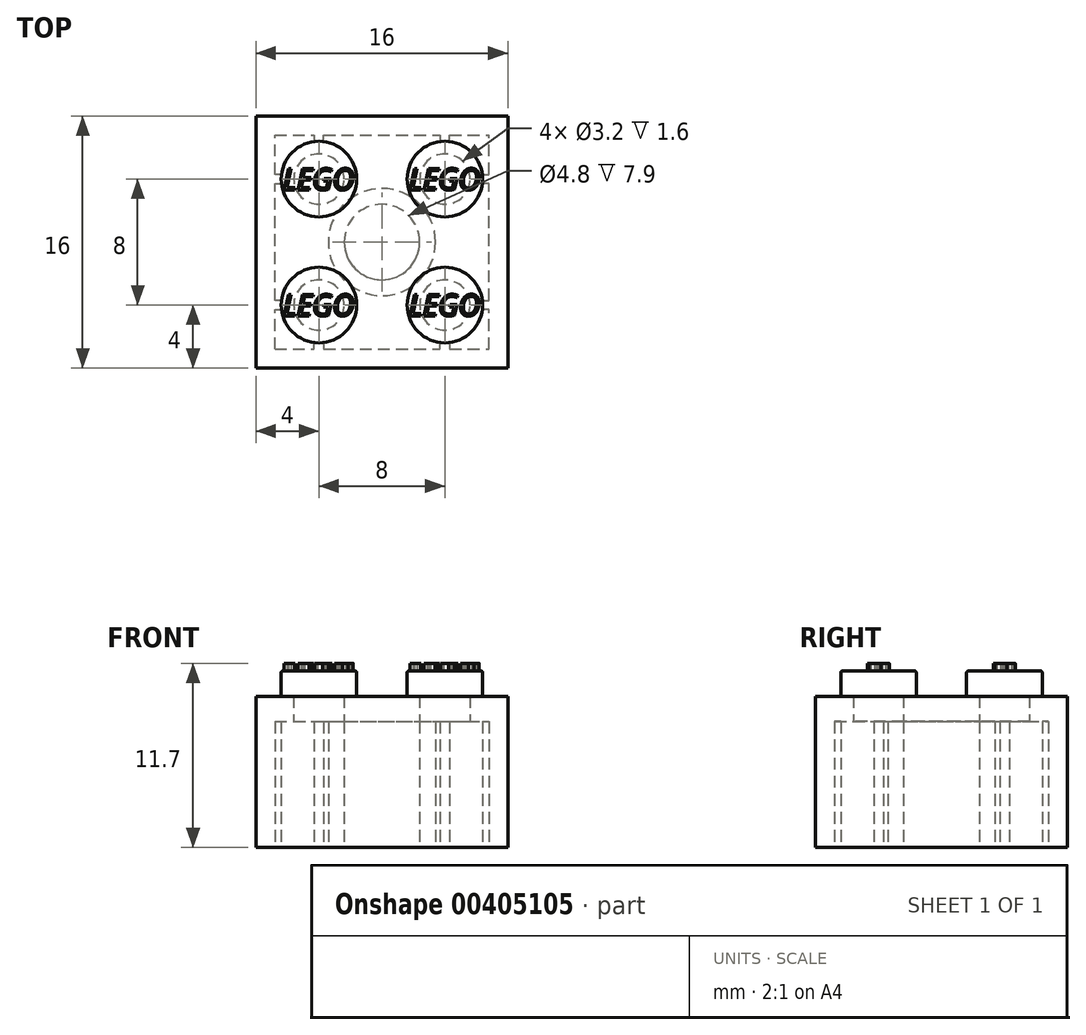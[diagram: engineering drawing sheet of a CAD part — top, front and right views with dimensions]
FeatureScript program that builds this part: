
annotation { "Feature Type Name" : "Feature", "Feature Type Description" : "" }
export const myFeature = defineFeature(function(context is Context, id is Id, definition is map)
    precondition{}
    {
        {
            var Q0;
            Q0=qCreatedBy(makeId("Top.planeOp"),FACE);
            var sketch = newSketch(context, id + "F0", { "sketchPlane" : qUnion([Q0])});
            skLineSegment(sketch, "E0.bottom", {"start": v(0, 0) * mm, "end": v(16, 0) * mm});
            skLineSegment(sketch, "E0.top", {"start": v(0, 16) * mm, "end": v(16, 16) * mm});
            skLineSegment(sketch, "E0.left", {"start": v(0, 0) * mm, "end": v(0, 16) * mm});
            skLineSegment(sketch, "E0.right", {"start": v(16, 0) * mm, "end": v(16, 16) * mm});
            skSolve(sketch);
        }
        {
            var Q0;
            Q0 = qSketchRegion(id + "F0", true);
            var Q1;
            Q1 = qConstructionFilter(qBodyType(qCreatedBy(id + "F0" ,EDGE), BodyType.WIRE), ConstructionObject.NO);
            extrude(context, id + "F1", {"entities" : qUnion([Q0]), "surfaceEntities" : qUnion([Q1]), "depth" : 9.6 * mm});
        }
        {
            var Q0;
            Q0=makeQuery(id+"F1.opExtrude","CAP_FACE",FACE,{"disambiguationData":[OSD([sQuery(id+"F0.wireOp",EDGE,"E0.bottom"),sQuery(id+"F0.wireOp",EDGE,"E0.top"),sQuery(id+"F0.wireOp",EDGE,"E0.left"),sQuery(id+"F0.wireOp",EDGE,"E0.right")])],"isStart":false});
            var sketch = newSketch(context, id + "F2", { "sketchPlane" : qUnion([Q0])});
            skLineSegment(sketch, "E1", {"start": v(0, 12) * mm, "end": v(16, 12) * mm, "construction": true});
            skLineSegment(sketch, "E2", {"start": v(4, 16) * mm, "end": v(4, 0) * mm, "construction": true});
            skLineSegment(sketch, "E3", {"start": v(12, 16) * mm, "end": v(12, 0) * mm, "construction": true});
            skLineSegment(sketch, "E4", {"start": v(0, 4) * mm, "end": v(16, 4) * mm, "construction": true});
            skCircle(sketch, "E5", {"center": v(4, 12) * mm, "radius": 2.4 * mm});
            skCircle(sketch, "E6", {"center": v(4, 4) * mm, "radius": 2.4 * mm});
            skCircle(sketch, "E7", {"center": v(12, 12) * mm, "radius": 2.4 * mm});
            skCircle(sketch, "E8", {"center": v(12, 4) * mm, "radius": 2.4 * mm});
            skSolve(sketch);
        }
        {
            var Q0;
            Q0 = qSketchRegion(id + "F2", true);
            extrude(context, id + "F3", {"entities" : qUnion([Q0]), "operationType" : NewBodyOperationType.ADD, "depth" : 1.6 * mm});
        }
        {
            var Q0;
            Q0=makeQuery(id+"F1.opExtrude","CAP_FACE",FACE,{"disambiguationData":[OSD([sQuery(id+"F0.wireOp",EDGE,"E0.bottom"),sQuery(id+"F0.wireOp",EDGE,"E0.top"),sQuery(id+"F0.wireOp",EDGE,"E0.left"),sQuery(id+"F0.wireOp",EDGE,"E0.right")])],"isStart":true});
            var sketch = newSketch(context, id + "F4", { "sketchPlane" : qUnion([Q0])});
            skLineSegment(sketch, "E9.bottom", {"start": v(0, 0) * mm, "end": v(16, 0) * mm, "construction": true});
            skLineSegment(sketch, "E9.top", {"start": v(0, -16) * mm, "end": v(16, -16) * mm, "construction": true});
            skLineSegment(sketch, "E9.left", {"start": v(0, 0) * mm, "end": v(0, -16) * mm, "construction": true});
            skLineSegment(sketch, "E9.right", {"start": v(16, 0) * mm, "end": v(16, -16) * mm, "construction": true});
            skLineSegment(sketch, "E10.0", {"start": v(1.2, -1.2) * mm, "end": v(14.8, -1.2) * mm});
            skLineSegment(sketch, "E10.1", {"start": v(1.2, -1.2) * mm, "end": v(1.2, -14.8) * mm});
            skLineSegment(sketch, "E10.2", {"start": v(1.2, -14.8) * mm, "end": v(14.8, -14.8) * mm});
            skLineSegment(sketch, "E10.3", {"start": v(14.8, -1.2) * mm, "end": v(14.8, -14.8) * mm});
            skLineSegment(sketch, "E11", {"start": v(1.2, -1.2) * mm, "end": v(14.8, -14.8) * mm, "construction": true});
            skLineSegment(sketch, "E12", {"start": v(1.2, -14.8) * mm, "end": v(14.8, -1.2) * mm, "construction": true});
            skCircle(sketch, "E13", {"center": v(8, -8) * mm, "radius": 3.4 * mm});
            skCircle(sketch, "E14", {"center": v(8, -8) * mm, "radius": 2.4 * mm});
            skLineSegment(sketch, "E15", {"start": v(1.2, -4) * mm, "end": v(14.8, -4) * mm, "construction": true});
            skLineSegment(sketch, "E16", {"start": v(14.8, -12) * mm, "end": v(1.2, -12) * mm, "construction": true});
            skLineSegment(sketch, "E17", {"start": v(4, -1.2) * mm, "end": v(4, -14.8) * mm, "construction": true});
            skLineSegment(sketch, "E18", {"start": v(12, -1.2) * mm, "end": v(12, -14.8) * mm, "construction": true});
            skLineSegment(sketch, "E19", {"start": v(3.7, -1.2) * mm, "end": v(3.7, -1.6) * mm});
            skLineSegment(sketch, "E20", {"start": v(3.7, -1.6) * mm, "end": v(4.3, -1.6) * mm});
            skLineSegment(sketch, "E21", {"start": v(4.3, -1.6) * mm, "end": v(4.3, -1.2) * mm});
            skLineSegment(sketch, "E22", {"start": v(11.7, -1.2) * mm, "end": v(11.7, -1.6) * mm});
            skLineSegment(sketch, "E23", {"start": v(11.7, -1.6) * mm, "end": v(12.3, -1.6) * mm});
            skLineSegment(sketch, "E24", {"start": v(12.3, -1.6) * mm, "end": v(12.3, -1.2) * mm});
            skLineSegment(sketch, "E25", {"start": v(1.2, -8) * mm, "end": v(14.8, -8) * mm, "construction": true});
            skLineSegment(sketch, "E26.MirrorCS", {"start": v(11.7, -14.8) * mm, "end": v(11.7, -14.4) * mm});
            skLineSegment(sketch, "E27.MirrorCS", {"start": v(11.7, -14.4) * mm, "end": v(12.3, -14.4) * mm});
            skLineSegment(sketch, "E28.MirrorCS", {"start": v(12.3, -14.4) * mm, "end": v(12.3, -14.8) * mm});
            skLineSegment(sketch, "E29.MirrorCS", {"start": v(4.3, -14.4) * mm, "end": v(4.3, -14.8) * mm});
            skLineSegment(sketch, "E30.MirrorCS", {"start": v(3.7, -14.8) * mm, "end": v(3.7, -14.4) * mm});
            skLineSegment(sketch, "E31.MirrorCS", {"start": v(3.7, -14.4) * mm, "end": v(4.3, -14.4) * mm});
            skLineSegment(sketch, "E32", {"start": v(8, -1.2) * mm, "end": v(8, -14.8) * mm, "construction": true});
            skLineSegment(sketch, "E33", {"start": v(1.2, -3.7) * mm, "end": v(1.6, -3.7) * mm});
            skLineSegment(sketch, "E34", {"start": v(1.6, -3.7) * mm, "end": v(1.6, -4.3) * mm});
            skLineSegment(sketch, "E35", {"start": v(1.6, -4.3) * mm, "end": v(1.2, -4.3) * mm});
            skLineSegment(sketch, "E36", {"start": v(1.2, -11.7) * mm, "end": v(1.6, -11.7) * mm});
            skLineSegment(sketch, "E37", {"start": v(1.6, -11.7) * mm, "end": v(1.6, -12.3) * mm});
            skLineSegment(sketch, "E38", {"start": v(1.6, -12.3) * mm, "end": v(1.2, -12.3) * mm});
            skLineSegment(sketch, "E39.MirrorCS", {"start": v(14.4, -12.3) * mm, "end": v(14.8, -12.3) * mm});
            skLineSegment(sketch, "E40.MirrorCS", {"start": v(14.4, -11.7) * mm, "end": v(14.4, -12.3) * mm});
            skLineSegment(sketch, "E41.MirrorCS", {"start": v(14.8, -11.7) * mm, "end": v(14.4, -11.7) * mm});
            skLineSegment(sketch, "E42.MirrorCS", {"start": v(14.4, -4.3) * mm, "end": v(14.8, -4.3) * mm});
            skLineSegment(sketch, "E43.MirrorCS", {"start": v(14.8, -3.7) * mm, "end": v(14.4, -3.7) * mm});
            skLineSegment(sketch, "E44.MirrorCS", {"start": v(14.4, -3.7) * mm, "end": v(14.4, -4.3) * mm});
            skSolve(sketch);
        }
        {
            var Q0;
            Q0=makeQuery(id+"F4.imprint","IMPRINT",FACE,{"disambiguationData":[TD([[makeQuery(id+"F4.imprint","IMPRINT",EDGE,{"derivedFrom":sQuery(id+"F4.wireOp",EDGE,"E10.0")}),-1.0]])]});
            var Q1;
            Q1=makeQuery(id+"F4.imprint","IMPRINT",FACE,{"disambiguationData":[TD([[makeQuery(id+"F4.imprint","IMPRINT",EDGE,{"derivedFrom":sQuery(id+"F4.wireOp",EDGE,"E14")}),1.0]])]});
            extrude(context, id + "F5", {"entities" : qUnion([Q0, Q1]), "operationType" : NewBodyOperationType.REMOVE, "oppositeDirection" : true, "depth" : 8 * mm});
        }
        {
            var Q0;
            Q0=makeQuery(id+"F5.boolean.opBoolean","COPY",FACE,{"derivedFrom":makeQuery(id+"F5.opExtrude","CAP_FACE",FACE,{"disambiguationData":[OSD([sQuery(id+"F4.wireOp",EDGE,"E10.0"),sQuery(id+"F4.wireOp",EDGE,"E10.1"),sQuery(id+"F4.wireOp",EDGE,"E10.2"),sQuery(id+"F4.wireOp",EDGE,"E10.3"),sQuery(id+"F4.wireOp",EDGE,"E13")])],"isStart":false})});
            var sketch = newSketch(context, id + "F6", { "sketchPlane" : qUnion([Q0])});
            skLineSegment(sketch, "E45", {"start": v(4, -1.2) * mm, "end": v(4, -14.8) * mm, "construction": true});
            skLineSegment(sketch, "E46", {"start": v(1.2, -12) * mm, "end": v(14.8, -12) * mm, "construction": true});
            skLineSegment(sketch, "E47", {"start": v(1.2, -4) * mm, "end": v(14.8, -4) * mm, "construction": true});
            skLineSegment(sketch, "E48", {"start": v(12, -14.8) * mm, "end": v(12, -1.2) * mm, "construction": true});
            skPoint(sketch, "E49", {"position": v(4, -1.2) * mm});
            skCircle(sketch, "E50", {"center": v(4, -4) * mm, "radius": 1.6 * mm});
            skCircle(sketch, "E51", {"center": v(12, -4) * mm, "radius": 1.6 * mm});
            skCircle(sketch, "E52", {"center": v(12, -12) * mm, "radius": 1.6 * mm});
            skCircle(sketch, "E53", {"center": v(4, -12) * mm, "radius": 1.6 * mm});
            skSolve(sketch);
        }
        {
            var Q0;
            Q0 = qSketchRegion(id + "F6", true);
            extrude(context, id + "F7", {"entities" : qUnion([Q0]), "operationType" : NewBodyOperationType.REMOVE, "oppositeDirection" : true, "depth" : 1.6 * mm});
        }
        {
            var Q0;
            Q0=makeQuery(id+"F3.opExtrude","CAP_FACE",FACE,{"disambiguationData":[OSD([sQuery(id+"F2.wireOp",EDGE,"E8")])],"isStart":false});
            var sketch = newSketch(context, id + "F8", { "sketchPlane" : qUnion([Q0])});
            skText(sketch, "E54", { "text": "LEGO", "fontName": "OpenSans-Italic.ttf"});
            skText(sketch, "E55", { "text": "LEGO", "fontName": "OpenSans-Italic.ttf"});
            skText(sketch, "E56", { "text": "LEGO", "fontName": "OpenSans-Italic.ttf"});
            skText(sketch, "E57", { "text": "LEGO", "fontName": "OpenSans-Italic.ttf"});
            const initialGuessF8  = {"E54": [0.0097, 0.00331, 1, 0, 0.00137], "E55": [0.0017, 0.00331, 1, 0, 0.00137], "E56": [0.0017, 0.01131, 1, 0, 0.00137], "E57": [0.0097, 0.01131, 1, 0, 0.00137]};
            skSetInitialGuess(sketch, initialGuessF8);
            skSolve(sketch);
        }
        {
            var Q0;
            Q0 = qSketchRegion(id + "F8", true);
            extrude(context, id + "F9", {"entities" : qUnion([Q0]), "operationType" : NewBodyOperationType.ADD, "depth" : .5 * mm});
        }
        {
            var Q0;
            Q0=makeQuery(id+"F3.opExtrude","CAP_EDGE",EDGE,{"disambiguationData":[OSD([sQuery(id+"F2.wireOp",EDGE,"E8")])],"isStart":false});
            var Q1;
            Q1=makeQuery(id+"F3.opExtrude","CAP_EDGE",EDGE,{"disambiguationData":[OSD([sQuery(id+"F2.wireOp",EDGE,"E6")])],"isStart":false});
            var Q2;
            Q2=makeQuery(id+"F3.opExtrude","CAP_EDGE",EDGE,{"disambiguationData":[OSD([sQuery(id+"F2.wireOp",EDGE,"E7")])],"isStart":false});
            var Q3;
            Q3=makeQuery(id+"F3.opExtrude","CAP_EDGE",EDGE,{"disambiguationData":[OSD([sQuery(id+"F2.wireOp",EDGE,"E5")])],"isStart":false});
            fillet(context, id + "F10", {"entities" : qUnion([Q0, Q1, Q2, Q3]), "radius" : .1 * mm, "tangentPropagation" : true, "allowEdgeOverflow" : false});
        }
        {
            var Q0;
            Q0=makeQuery(id+"F5.boolean.opBoolean","COPY",EDGE,{"derivedFrom":makeQuery(id+"F5.opExtrude","CAP_EDGE",EDGE,{"disambiguationData":[OSD([sQuery(id+"F4.wireOp",EDGE,"E14")])],"isStart":true})});
            fillet(context, id + "F11", {"entities" : qUnion([Q0]), "radius" : .1 * mm, "tangentPropagation" : true, "allowEdgeOverflow" : false});
        }
    });
